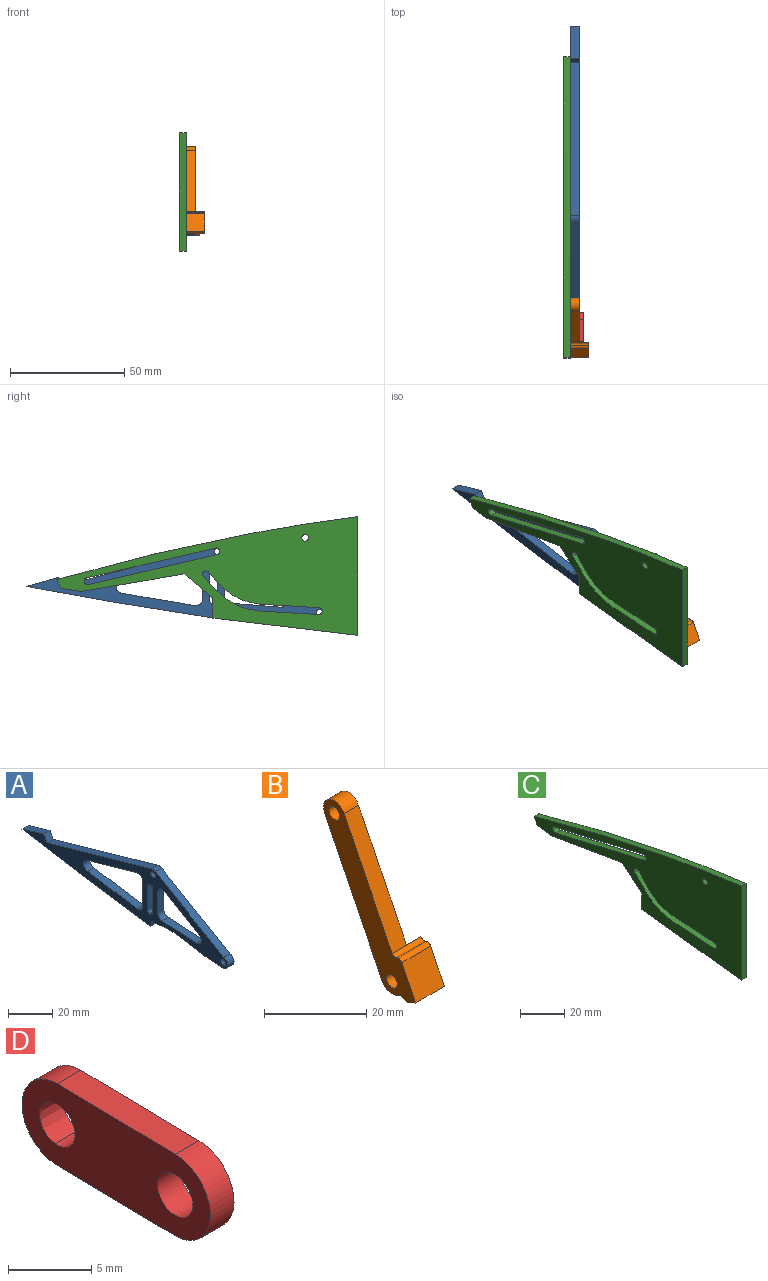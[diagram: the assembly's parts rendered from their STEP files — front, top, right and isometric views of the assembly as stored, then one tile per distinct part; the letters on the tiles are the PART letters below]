
ASSEMBLY  parts=4 mates=4
PART A: 36 faces, bbox 4x131.8x32.2 mm
  f0: plane 31.99x9.12mm, normal (0,-0.27,-0.96), area 133mm2, adj f1,f33,f34,f35
  f1: cylinder r=3mm len=5.85mm, axis (-1,0,0), area 32.5mm2, adj f0,f2,f34,f35
  f2: plane 31.99x4.91mm, normal (0,-0.15,0.99), area 129.4mm2, adj f1,f3,f34,f35
  f3: cylinder r=3mm len=4mm, axis (-1,0,0), area 20.7mm2, adj f2,f4,f34,f35
  f4: plane 14.03x4mm, normal (0,1,0), area 56.1mm2, adj f3,f33,f34,f35
  f5: plane 11.5x4mm, normal (0,-1,0), area 46mm2, adj f6,f28,f34,f35
  f6: cylinder r=3mm len=4mm, axis (-1,0,0), area 18.1mm2, adj f5,f7,f34,f35
  f7: plane 21.95x4mm, normal (0,-0.06,1), area 88mm2, adj f6,f8,f34,f35
  f8: cylinder r=3mm len=5.59mm, axis (-1,0,0), area 32.1mm2, adj f7,f9,f34,f35
  f9: plane 21.95x12.91mm, normal (0,0.51,-0.86), area 101.9mm2, adj f8,f28,f34,f35
  f10: extruded ~4x2.96mm, area 18.8mm2, adj f29,f34,f35
  f11: extruded ~4x2.99mm, area 18.8mm2, adj f30,f34,f35
  f12: cylinder r=1.5mm len=4mm, axis (-1,0,0), area 9.4mm2, adj f13,f31,f34,f35
  f13: plane 13.36x4mm, normal (0,-1,0), area 53.4mm2, adj f12,f14,f34,f35
  f14: cylinder r=1.5mm len=4mm, axis (-1,0,0), area 9.4mm2, adj f13,f15,f34,f35
  f15: plane 4x0.45mm, normal (0,0,1), area 1.8mm2, adj f14,f16,f34,f35
  f16: cylinder r=1.5mm len=4mm, axis (-1,0,0), area 9.4mm2, adj f15,f17,f34,f35
  f17: plane 13.36x4mm, normal (0,1,0), area 53.4mm2, adj f16,f18,f34,f35
  f18: cylinder r=1.5mm len=4mm, axis (-1,0,0), area 9.4mm2, adj f17,f31,f34,f35
  f19: extruded ~45.79x4mm, area 184.5mm2, adj f20,f32,f34,f35
  f20: plane 4x3.01mm, normal (0,-0.99,-0.15), area 12.2mm2, adj f19,f21,f34,f35
  f21: extruded ~82.5x12.67mm, area 333.9mm2, adj f20,f22,f34,f35
  f22: extruded ~13.99x4.19mm, area 58.4mm2, adj f21,f23,f34,f35
  f23: plane 4x3.86mm, normal (0,-0.88,0.47), area 17.5mm2, adj f22,f24,f34,f35
  f24: plane 66.78x19.04mm, normal (0,0.27,0.96), area 277.8mm2, adj f23,f25,f34,f35
  f25: cylinder r=3mm len=4mm, axis (-1,0,0), area 10.8mm2, adj f24,f26,f34,f35
  f26: plane 43.82x25.77mm, normal (0,-0.51,0.86), area 203.3mm2, adj f25,f27,f34,f35
  f27: cylinder r=3mm len=5.97mm, axis (-1,0,0), area 36.9mm2, adj f26,f32,f34,f35
  f28: cylinder r=3mm len=4.52mm, axis (-1,0,0), area 25.2mm2, adj f5,f9,f34,f35
  f29: cylinder r=1.5mm len=4mm, axis (-1,0,0), area 18.8mm2, adj f10,f34,f35
  f30: cylinder r=1.5mm len=4mm, axis (-1,0,0), area 18.8mm2, adj f11,f34,f35
  f31: plane 4x0.45mm, normal (0,0,-1), area 1.8mm2, adj f12,f18,f34,f35
  f32: plane 4x0.11mm, normal (0,-0.06,1), area 0.4mm2, adj f19,f27,f34,f35
  f33: cylinder r=3mm len=4mm, axis (-1,0,0), area 22.2mm2, adj f0,f4,f34,f35
  f34: plane 131.84x32.23mm, normal (1,0,0), area 1168.1mm2, adj f0,f1,f2,f3,f4,f5,f6,f7
  f35: plane 131.84x32.23mm, normal (-1,0,0), area 1168.1mm2, adj f0,f1,f2,f3,f4,f5,f6,f7
PART B: 16 faces, bbox 8x25.5x38.3 mm
  f0: plane 26.92x13.29mm, normal (0,-0.9,0.44), area 120.1mm2, adj f5,f7,f8,f10
  f1: plane 4x1.2mm, normal (0,-0.44,-0.9), area 5.4mm2, adj f2,f7,f8,f15
  f2: cylinder r=3mm len=4mm, axis (-1,0,0), area 17.5mm2, adj f1,f3,f7,f8
  f3: plane 32.31x15.94mm, normal (0,0.9,-0.44), area 144.1mm2, adj f2,f5,f7,f8
  f4: cylinder r=1.5mm len=4mm, axis (-1,0,0), area 37.7mm2, adj f7,f8
  f5: cylinder r=3mm len=5.69mm, axis (-1,0,0), area 37.7mm2, adj f0,f3,f7,f8
  f6: cylinder r=1.5mm len=4mm, axis (-1,0,0), area 37.7mm2, adj f7,f8
  f7: plane 38.31x23.68mm, normal (1,0,0), area 234.1mm2, adj f0,f1,f2,f3,f4,f5,f6,f9
  f8: plane 38.31x25.48mm, normal (-1,0,0), area 253.4mm2, adj f0,f1,f2,f3,f4,f5,f6,f10
  f9: plane 9.53x4.7mm, normal (0,0.9,-0.44), area 42.5mm2, adj f7,f10,f13,f14
  f10: cylinder r=1mm len=8mm, axis (-1,0,0), area 12.6mm2, adj f0,f8,f9,f11,f14
  f11: cylinder r=1mm len=8mm, axis (-1,0,0), area 12.6mm2, adj f8,f10,f12,f14
  f12: plane 8x7.74mm, normal (0,-0.9,0.44), area 69mm2, adj f8,f11,f13,f14
  f13: plane 8x2.11mm, normal (0,-0.44,-0.9), area 17.4mm2, adj f7,f8,f9,f12,f14,f15
  f14: plane 9.53x6.5mm, normal (1,0,0), area 19.3mm2, adj f9,f10,f11,f12,f13
  f15: plane 4x2.21mm, normal (0,0.32,-0.95), area 9.3mm2, adj f1,f7,f8,f13
PART C: 19 faces, bbox 3x132x52 mm
  f0: plane 3.86x3mm, normal (0,0.88,-0.47), area 13.1mm2, adj f1,f16,f17,f18
  f1: extruded ~132.05x27.6mm, area 405.1mm2, adj f0,f2,f17,f18
  f2: plane 52x3mm, normal (0,-1,0), area 156mm2, adj f1,f3,f17,f18
  f3: extruded ~63.54x7.55mm, area 192mm2, adj f2,f4,f17,f18
  f4: plane 8.86x3mm, normal (0,1,0), area 26.6mm2, adj f3,f5,f17,f18
  f5: plane 12.58x10.56mm, normal (0,0.64,-0.77), area 49.3mm2, adj f4,f6,f17,f18
  f6: plane 44.91x7.76mm, normal (0,-0.17,-0.99), area 136.7mm2, adj f5,f16,f17,f18
  f7: cylinder r=1.5mm len=3mm, axis (-1,0,0), area 14.1mm2, adj f8,f13,f17,f18
  f8: plane 56.41x13.08mm, normal (0,-0.23,-0.97), area 173.7mm2, adj f7,f9,f17,f18
  f9: cylinder r=1.5mm len=3mm, axis (-1,0,0), area 14.1mm2, adj f8,f13,f17,f18
  f10: cylinder r=1.5mm len=3mm, axis (-1,0,0), area 14.1mm2, adj f11,f14,f17,f18
  f11: extruded ~48.5x15.63mm, area 160.2mm2, adj f10,f12,f17,f18
  f12: cylinder r=1.5mm len=3mm, axis (-1,0,0), area 14.2mm2, adj f11,f14,f17,f18
  f13: plane 56.41x13.08mm, normal (0,0.23,0.97), area 173.7mm2, adj f7,f9,f17,f18
  f14: extruded ~50.36x16.6mm, area 166.6mm2, adj f10,f12,f17,f18
  f15: cylinder r=1.5mm len=3mm, axis (-1,0,0), area 28.3mm2, adj f17,f18
  f16: plane 8.96x3mm, normal (0,0.15,-0.99), area 27.2mm2, adj f0,f6,f17,f18
  f17: plane 132.05x52mm, normal (1,0,0), area 3158.5mm2, adj f0,f1,f2,f3,f4,f5,f6,f7
  f18: plane 132.05x52mm, normal (-1,0,0), area 3158.5mm2, adj f0,f1,f2,f3,f4,f5,f6,f7
PART D: 9 faces, bbox 2x16x6.2 mm
  f0: cylinder r=1.5mm len=2.99mm, axis (-1,0,0), area 9.4mm2, adj f6,f7,f8
  f1: plane 9.91x2mm, normal (0,0.02,-1), area 19.8mm2, adj f2,f5,f7,f8
  f2: cylinder r=3mm len=6mm, axis (-1,0,0), area 18.8mm2, adj f1,f3,f7,f8
  f3: plane 10.02x2mm, normal (0,-0.02,1), area 20mm2, adj f2,f5,f7,f8
  f4: cylinder r=1.5mm len=3mm, axis (-1,0,0), area 18.8mm2, adj f7,f8
  f5: cylinder r=3mm len=6mm, axis (-1,0,0), area 19mm2, adj f1,f3,f7,f8
  f6: extruded ~2.99x2mm, area 9.4mm2, adj f0,f7,f8
  f7: plane 16x6.18mm, normal (1,0,0), area 74.1mm2, adj f0,f1,f2,f3,f4,f5,f6
  f8: plane 16x6.18mm, normal (-1,0,0), area 74.1mm2, adj f0,f1,f2,f3,f4,f5,f6
PLACE A rot(axis=(1,0,0),0.8deg) t=(1.5,-34.9,80.69)mm
PLACE B rot(axis=(-1,0,0),0.7deg) t=(1.5,-34.96,82.01)mm
PLACE C t=(-1.5,-34.54,81.66)mm fixed
PLACE D rot(axis=(-1,0,0),4.8deg) t=(1.5,-35.12,82.93)mm
MATE revolute B.f4 <-> C.f15  axis (-1,0,0) through (1.5,-6.02,116.79)mm
MATE revolute A.f27 <-> D.f0  axis (1,0,0) through (5.5,-12.37,84.01)mm
MATE pin_slot A.f25 <-> C.f7  axis (-1,0,0) through (1.5,32.18,110.83)mm
MATE revolute B.f2 <-> D.f4  axis (1,0,0) through (5.5,-22.35,84.68)mm
